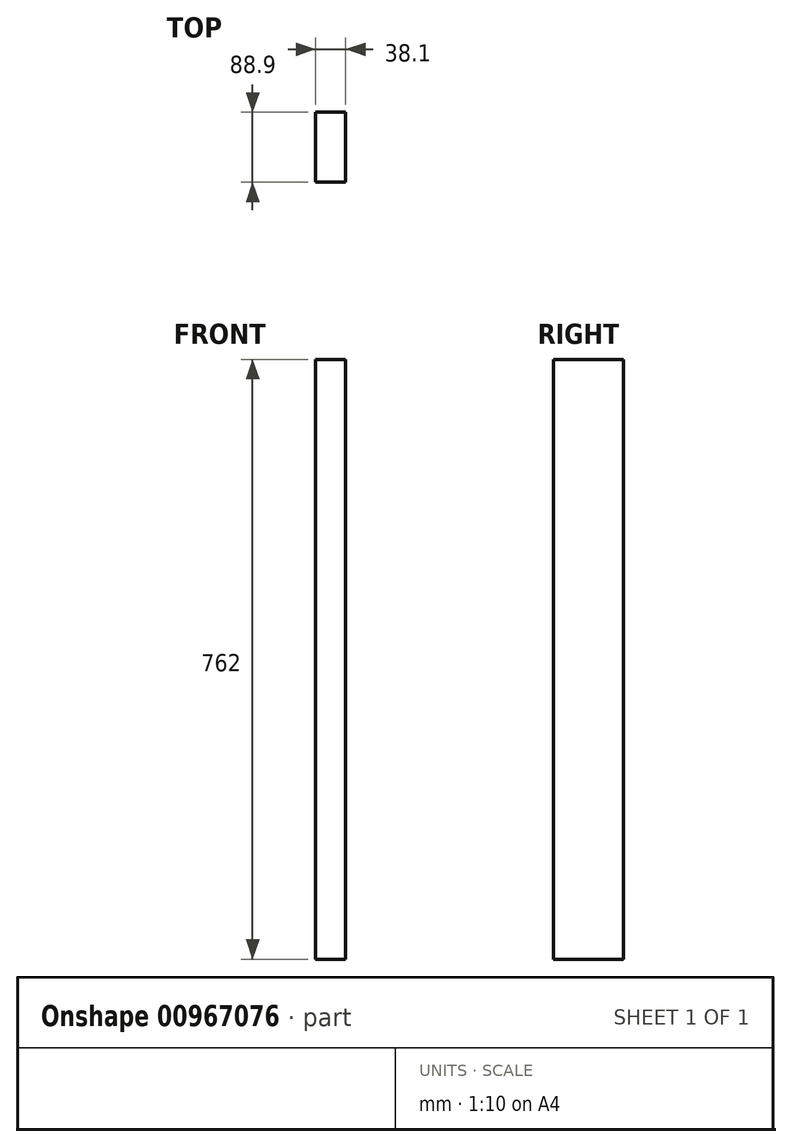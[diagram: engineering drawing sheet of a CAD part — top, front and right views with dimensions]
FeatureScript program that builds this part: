
annotation { "Feature Type Name" : "Feature", "Feature Type Description" : "" }
export const myFeature = defineFeature(function(context is Context, id is Id, definition is map)
    precondition{}
    {
        {
            var Q0;
            Q0=qCreatedBy(makeId("Top.planeOp"),FACE);
            var sketch = newSketch(context, id + "F0", { "sketchPlane" : qUnion([Q0])});
            skLineSegment(sketch, "E0.bottom", {"start": v(0, 0) * mm, "end": v(-38.1, 0) * mm});
            skLineSegment(sketch, "E0.top", {"start": v(0, 88.9) * mm, "end": v(-38.1, 88.9) * mm});
            skLineSegment(sketch, "E0.left", {"start": v(0, 0) * mm, "end": v(0, 88.9) * mm});
            skLineSegment(sketch, "E0.right", {"start": v(-38.1, 0) * mm, "end": v(-38.1, 88.9) * mm});
            skSolve(sketch);
        }
        {
            var Q0;
            Q0=qSketchRegion(id+"F0",true);
            extrude(context, id + "F1", {"entities" : qUnion([Q0]), "depth" : 762 * mm, "offsetDistance" : 25.4 * mm});
        }
    });
